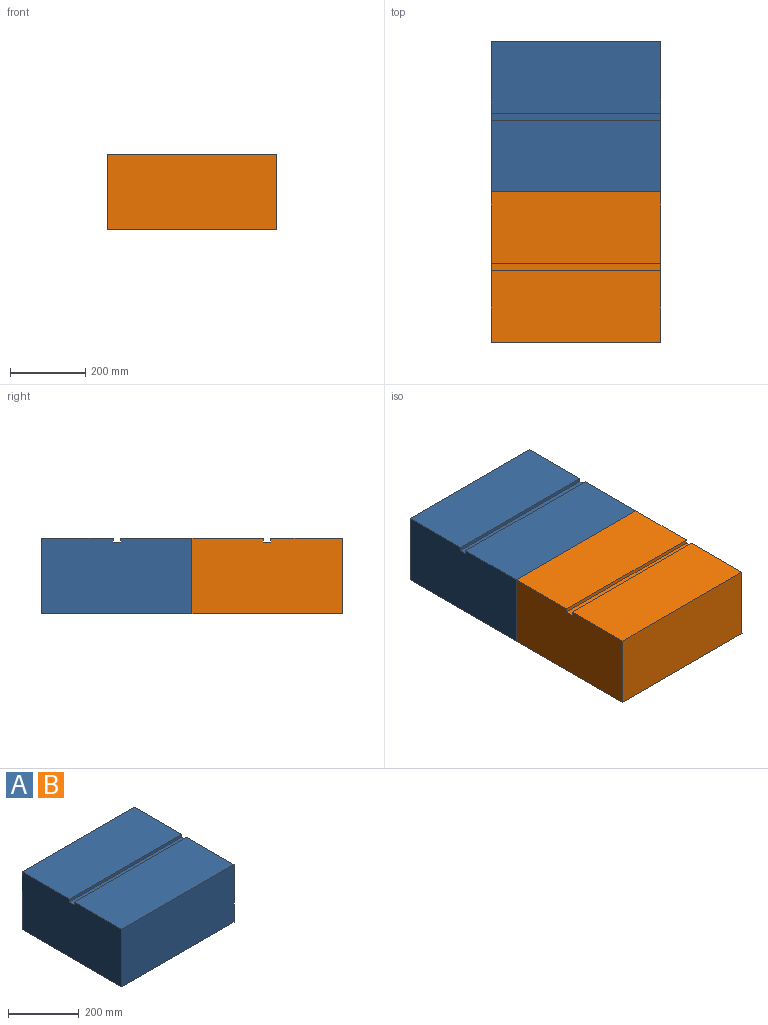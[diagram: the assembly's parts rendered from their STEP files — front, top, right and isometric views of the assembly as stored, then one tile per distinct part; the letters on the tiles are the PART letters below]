
ASSEMBLY  parts=2 mates=1
PART A: 10 faces, bbox 450x400x200 mm
  f0: plane 450x190mm, normal (0,0,1), area 85500mm2, adj f1,f2,f3,f8
  f1: plane 400x200mm, normal (-1,0,0), area 79800mm2, adj f0,f3,f4,f5,f6,f7,f8,f9
  f2: plane 400x200mm, normal (1,0,0), area 79800mm2, adj f0,f3,f4,f5,f6,f7,f8,f9
  f3: plane 450x200mm, normal (0,-1,0), area 90000mm2, adj f0,f1,f2,f4
  f4: plane 450x400mm, normal (0,0,-1), area 180000mm2, adj f1,f2,f3,f5
  f5: plane 450x200mm, normal (0,1,0), area 90000mm2, adj f1,f2,f4,f6
  f6: plane 450x190mm, normal (0,0,1), area 85500mm2, adj f1,f2,f5,f7
  f7: plane 450x10mm, normal (0,-1,0), area 4500mm2, adj f1,f2,f6,f9
  f8: plane 450x10mm, normal (0,1,0), area 4500mm2, adj f0,f1,f2,f9
  f9: plane 450x20mm, normal (0,0,1), area 9000mm2, adj f1,f2,f7,f8
PART B: same geometry as A
PLACE A t=(82.14,591.77,419.71)mm
PLACE B t=(82.14,191.77,419.71)mm
MATE fastened B.f5 <-> A.f3  axis (0,1,0) through (82.14,431.16,483.27)mm
